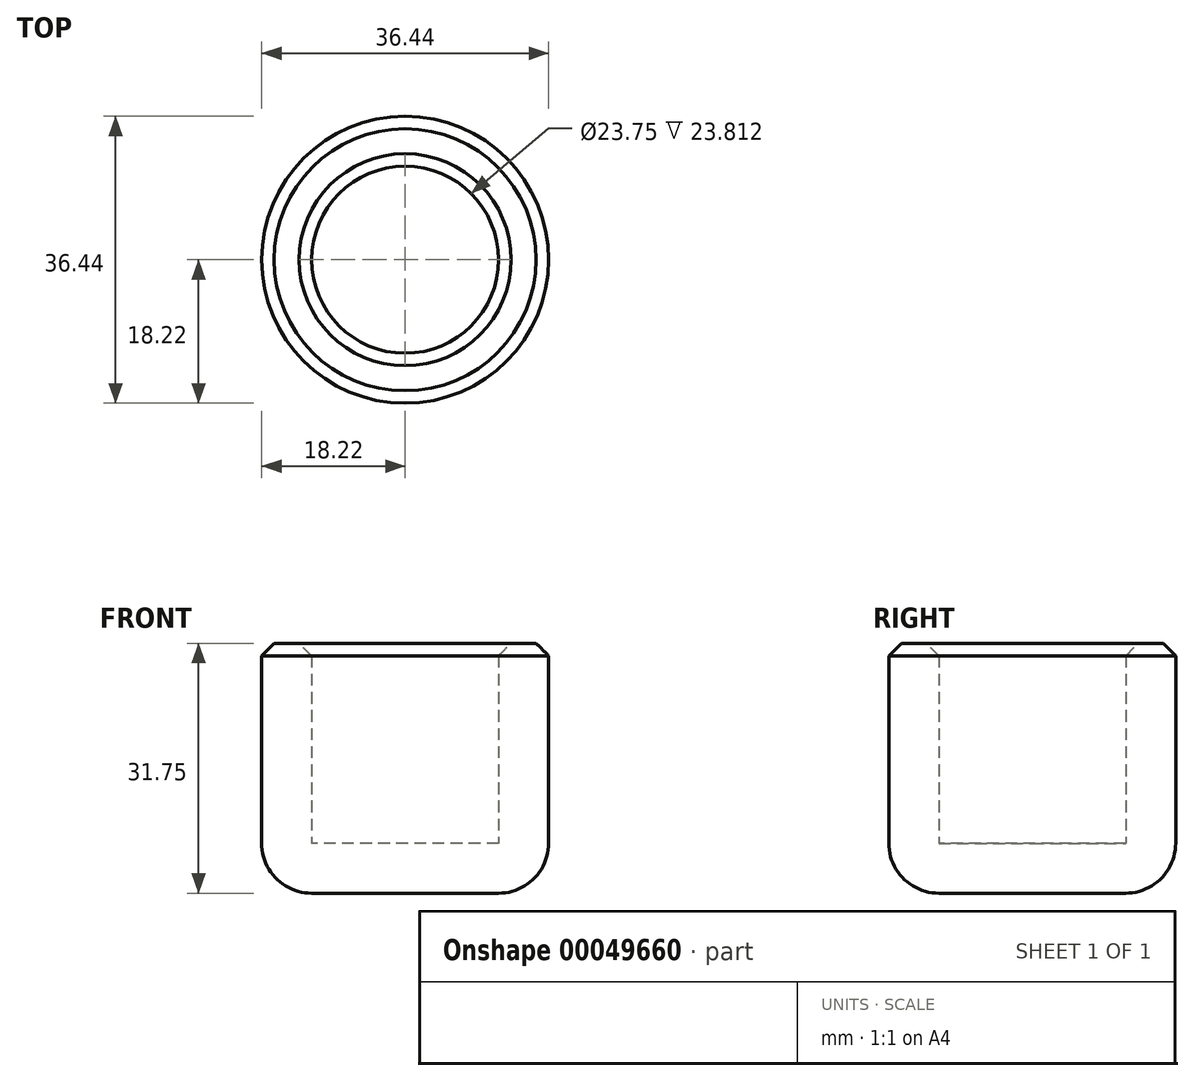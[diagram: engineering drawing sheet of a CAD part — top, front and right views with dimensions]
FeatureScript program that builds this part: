
annotation { "Feature Type Name" : "Feature", "Feature Type Description" : "" }
export const myFeature = defineFeature(function(context is Context, id is Id, definition is map)
    precondition{}
    {
        {
            var Q0;
            Q0=qCreatedBy(makeId("Top.planeOp"),FACE);
            var sketch = newSketch(context, id + "F0", { "sketchPlane" : qUnion([Q0])});
            skCircle(sketch, "E0", {"center": v(0, 0) * mm, "radius": 18.22 * mm});
            skSolve(sketch);
        }
        {
            var Q0;
            Q0=makeQuery(id+"F0.imprint","IMPRINT",FACE,{"disambiguationData":[TD([[makeQuery(id+"F0.imprint","IMPRINT",EDGE,{"derivedFrom":sQuery(id+"F0.wireOp",EDGE,"E0")}),1.0]])]});
            extrude(context, id + "F1", {"entities" : qUnion([Q0]), "depth" : 31.75 * mm});
        }
        {
            var Q0;
            Q0=makeQuery(id+"F1.opExtrude","CAP_FACE",FACE,{"disambiguationData":[OSD([sQuery(id+"F0.wireOp",EDGE,"E0")])],"isStart":false});
            shell(context, id + "F2", {"entities" : qUnion([Q0]), "thickness" : 6.35 * mm});
        }
        {
            var Q0;
            Q0=makeQuery(id+"F1.opExtrude","CAP_EDGE",EDGE,{"disambiguationData":[OSD([sQuery(id+"F0.wireOp",EDGE,"E0")])],"isStart":true});
            fillet(context, id + "F3", {"entities" : qUnion([Q0]), "radius" : 6.35 * mm, "tangentPropagation" : true, "allowEdgeOverflow" : false});
        }
        {
            var Q0;
            Q0=makeQuery(id+"F1.opExtrude","CAP_FACE",FACE,{"disambiguationData":[OSD([sQuery(id+"F0.wireOp",EDGE,"E0")])],"isStart":false});
            chamfer(context, id + "F4", {"entities" : qUnion([Q0]), "width" : 1.59 * mm, "tangentPropagation" : true});
        }
    });
